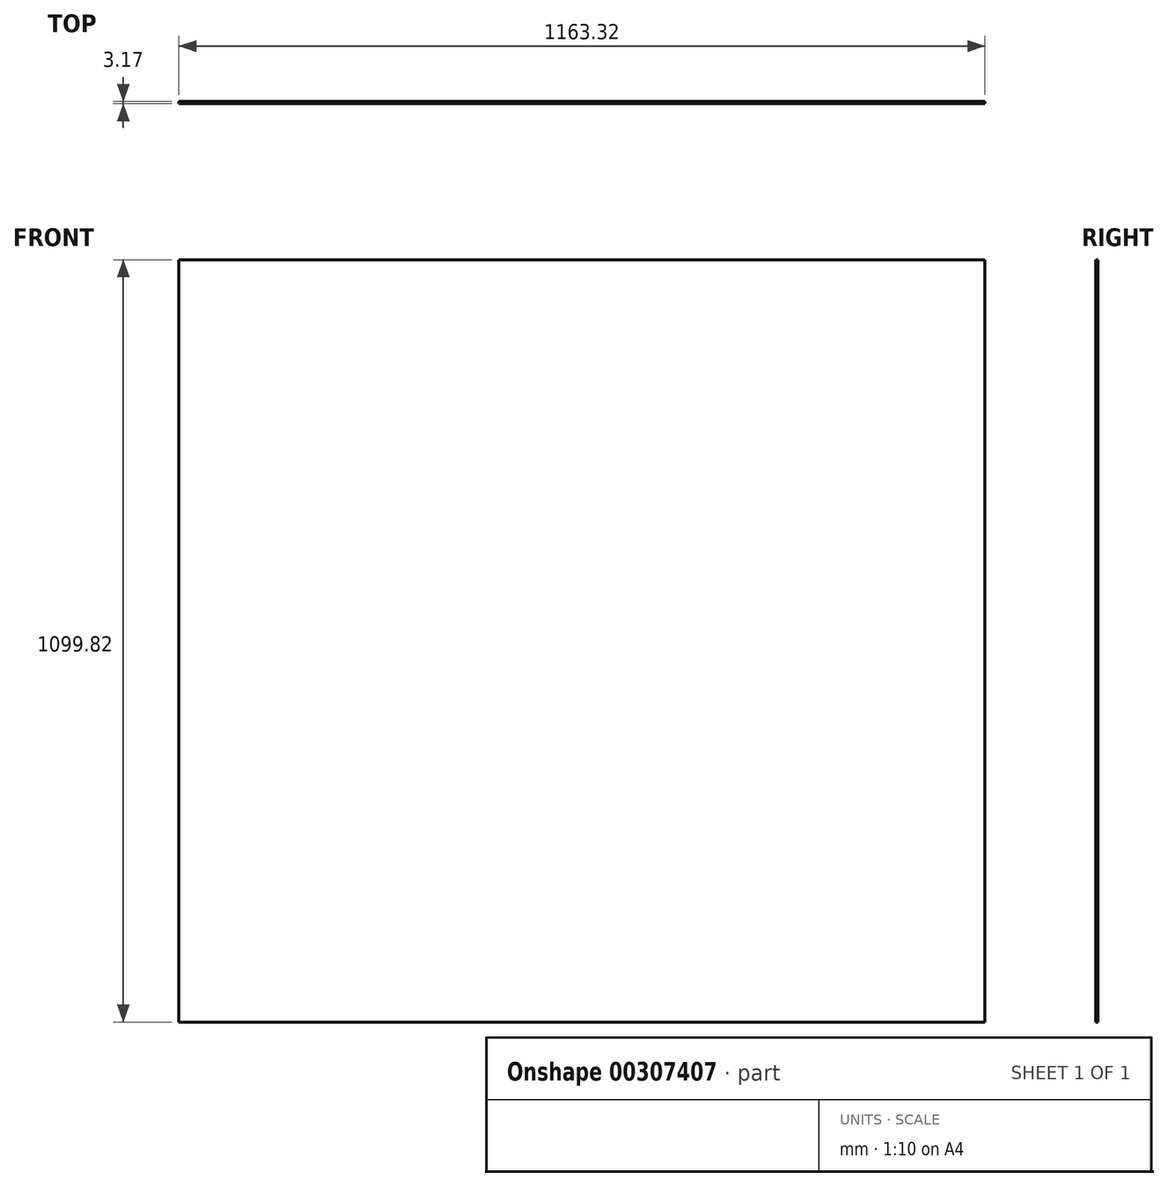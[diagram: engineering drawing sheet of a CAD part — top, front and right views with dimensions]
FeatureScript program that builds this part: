
annotation { "Feature Type Name" : "Feature", "Feature Type Description" : "" }
export const myFeature = defineFeature(function(context is Context, id is Id, definition is map)
    precondition{}
    {
        {
            var Q0;
            Q0=qCreatedBy(makeId("Front.planeOp"),FACE);
            var sketch = newSketch(context, id + "F0", { "sketchPlane" : qUnion([Q0])});
            skLineSegment(sketch, "E0.bottom", {"start": v(581.66, 549.9) * mm, "end": v(-581.66, 549.9) * mm});
            skLineSegment(sketch, "E0.top", {"start": v(581.66, -549.9) * mm, "end": v(-581.66, -549.9) * mm});
            skLineSegment(sketch, "E0.left", {"start": v(581.66, 549.9) * mm, "end": v(581.66, -549.9) * mm});
            skLineSegment(sketch, "E0.right", {"start": v(-581.66, 549.9) * mm, "end": v(-581.66, -549.9) * mm});
            skPoint(sketch, "E0.middle", {"position": v(0, 0) * mm});
            skSolve(sketch);
        }
        {
            var Q0;
            Q0=qSketchRegion(id+"F0",true);
            extrude(context, id + "F1", {"entities" : qUnion([Q0]), "depth" : 3.17 * mm});
        }
    });
